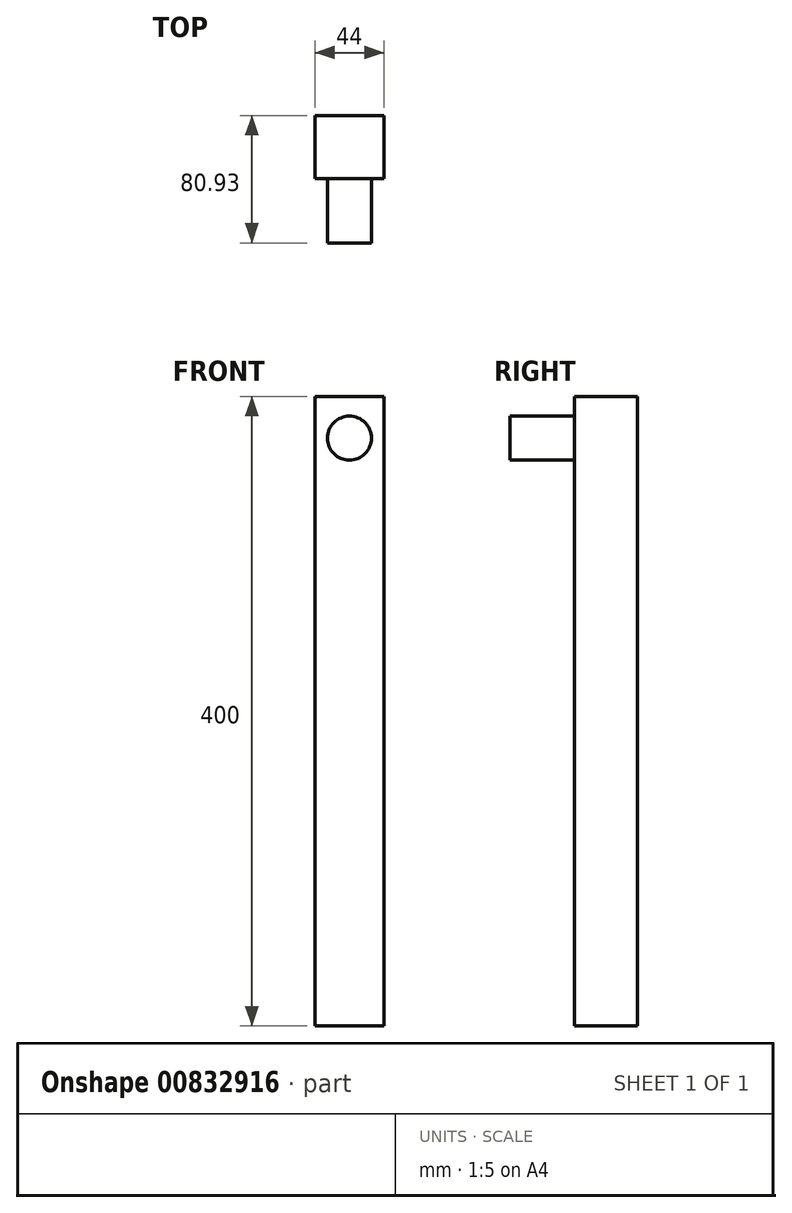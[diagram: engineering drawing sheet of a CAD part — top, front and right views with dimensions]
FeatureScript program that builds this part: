
annotation { "Feature Type Name" : "Feature", "Feature Type Description" : "" }
export const myFeature = defineFeature(function(context is Context, id is Id, definition is map)
    precondition{}
    {
        {
            var Q0;
            Q0=qCreatedBy(makeId("Top.planeOp"),FACE);
            var sketch = newSketch(context, id + "F0", { "sketchPlane" : qUnion([Q0])});
            skLineSegment(sketch, "E0.bottom", {"start": v(-22, 20.93) * mm, "end": v(22, 20.93) * mm});
            skLineSegment(sketch, "E0.top", {"start": v(-22, -19.07) * mm, "end": v(22, -19.07) * mm});
            skLineSegment(sketch, "E0.left", {"start": v(-22, 20.93) * mm, "end": v(-22, -19.07) * mm});
            skLineSegment(sketch, "E0.right", {"start": v(22, 20.93) * mm, "end": v(22, -19.07) * mm});
            skSolve(sketch);
        }
        {
            var Q0;
            Q0=makeQuery(id+"F0.imprint","IMPRINT",FACE,{"disambiguationData":[TD([[makeQuery(id+"F0.imprint","IMPRINT",EDGE,{"derivedFrom":sQuery(id+"F0.wireOp",EDGE,"E0.bottom")}),-1.0]])]});
            extrude(context, id + "F1", {"entities" : qUnion([Q0]), "depth" : 400 * mm, "offsetDistance" : 25 * mm});
        }
        {
            var Q0;
            Q0=qCreatedBy(makeId("Front.planeOp"),FACE);
            cPlane(context, id + "F2", {"entities" : qUnion([Q0]), "cplaneType" : CPlaneType.OFFSET, "offset" : 60 * mm, "width" : 150 * mm, "height" : 150 * mm});
        }
        {
            var Q0;
            Q0=qCreatedBy(id+"F2.planeOp",FACE);
            var sketch = newSketch(context, id + "F3", { "sketchPlane" : qUnion([Q0])});
            skCircle(sketch, "E1", {"center": v(0, 373.44) * mm, "radius": 14 * mm});
            skSolve(sketch);
        }
        {
            var Q0;
            Q0 = qSketchRegion(id + "F3", true);
            extrude(context, id + "F4", {"entities" : qUnion([Q0]), "operationType" : NewBodyOperationType.ADD, "endBound" : BoundingType.UP_TO_NEXT, "oppositeDirection" : true, "depth" : 25 * mm, "offsetDistance" : 25 * mm});
        }
    });
